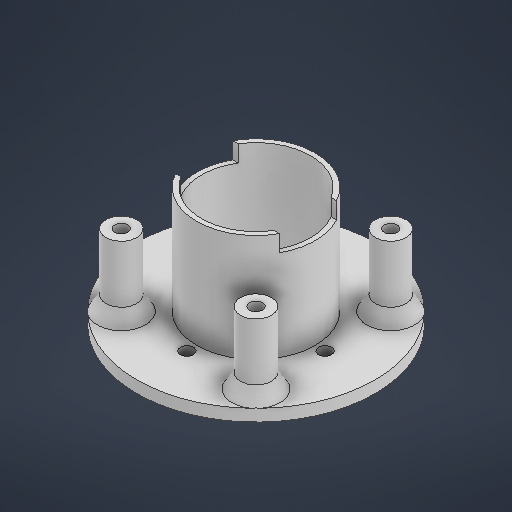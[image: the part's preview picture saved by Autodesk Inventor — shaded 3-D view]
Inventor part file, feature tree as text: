
AUTODESK INVENTOR PART (.ipt)
format: ipt  version: 2025 (Build 290162000, 162)  size: 412,160 bytes
history: native  units: in
note: dims shown in document units (in); Inventor stores cm internally (conversion verified against a paired STEP export)
features: sketch x11, extrude x7, chamfer x1
ambient origin geometry x8: Origin, YZ Plane, XZ Plane, XY Plane, X Axis, Y Axis, Z Axis, Center Point
bodies: Solid1 (feature_tree)
feature tree (19):
  sketch  "Sketch1"  dims[d0=3.937in d1=3.1496in]
  extrude  "Extrusion1"  Depth=3.1496in
  extrude  "Extrusion2"  Depth=3.1496in TaperAngle=360.0deg
  extrude  "Extrusion3"  Depth=0.0787in
  extrude  "Extrusion4"  Depth=0.1969in TaperAngle=0.0deg
  extrude  "Extrusion5"  Depth=1.6969in TaperAngle=0.0deg
  extrude  "Extrusion6"  Depth=0.2165in
  extrude  "Extrusion7"  Depth=1.6969in TaperAngle=0.0deg
  chamfer  "Chamfer1"  Distance=3.1496in Angle=360.0deg
  sketch  "Sketch Circular Pattern1"  dims[d2=0.2165in d3=3.1496in d5=360.0deg]
  sketch  "Sketch2"  dims[d7=1.8031in d8=0.0787in]
  sketch  "Sketch Circular Pattern2"  dims[d9=0.9449in d10=0.1969in d11=0.0in]
  sketch  "Sketch3"  dims[d12=1.9724in d13=0.0in d14=1.6969in d15=0.0in]
  sketch  "Sketch Circular Pattern5"  dims[d18=1.5748in d20=360.0deg d22=1.6969in d23=0.0in]
  sketch  "Sketch Circular Pattern6"  dims[d29=0.315in d34=3.1496in d36=360.0deg]
  sketch  "Sketch4"  dims[d16=2.2835in d17=0.2165in]
  sketch  "Sketch Circular Pattern7"  dims[d38=0.2165in]
  sketch  "Sketch5"  dims[d24=0.5118in]
  sketch  "Sketch Circular Pattern8"  dims[d39=3.1496in d41=360.0deg d43=0.5906in d44=0.0in d45=0.315in d46=3.1496in d48=360.0deg d50=0.1969in d51=0.0in d52=0.2165in d53=3.1496in d55=360.0deg d57=0.3937in d58=0.0in d59=0.1412in d60=0.2362in d61=45.0deg]
